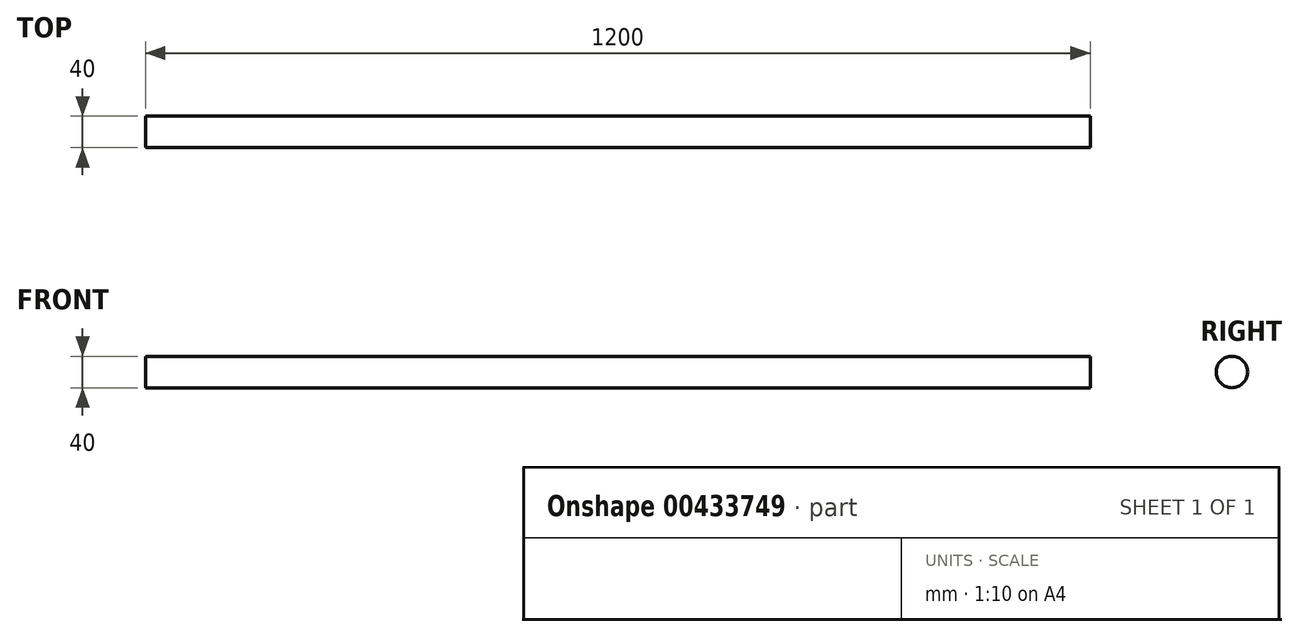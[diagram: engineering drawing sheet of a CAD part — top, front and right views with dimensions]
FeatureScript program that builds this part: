
annotation { "Feature Type Name" : "Feature", "Feature Type Description" : "" }
export const myFeature = defineFeature(function(context is Context, id is Id, definition is map)
    precondition{}
    {
        {
            var Q0;
            Q0=qCreatedBy(makeId("Front.planeOp"),FACE);
            var sketch = newSketch(context, id + "F0", { "sketchPlane" : qUnion([Q0])});
            skLineSegment(sketch, "E0.bottom", {"start": v(-558.88, -42.5) * mm, "end": v(641.12, -42.5) * mm});
            skLineSegment(sketch, "E0.top", {"start": v(-558.88, -82.5) * mm, "end": v(641.12, -82.5) * mm});
            skLineSegment(sketch, "E0.left", {"start": v(-558.88, -42.5) * mm, "end": v(-558.88, -82.5) * mm});
            skLineSegment(sketch, "E0.right", {"start": v(641.12, -42.5) * mm, "end": v(641.12, -82.5) * mm});
            skSolve(sketch);
        }
        {
            var Q0;
            Q0 = qSketchRegion(id + "F0", true);
            extrude(context, id + "F1", {"entities" : qUnion([Q0]), "depth" : 40 * mm, "offsetDistance" : 25 * mm});
        }
        {
            var Q0;
            Q0=makeQuery(id+"F1.opExtrude","CAP_EDGE",EDGE,{"disambiguationData":[OSD([sQuery(id+"F0.wireOp",EDGE,"E0.bottom")])],"isStart":false});
            var Q1;
            Q1=makeQuery(id+"F1.opExtrude","CAP_EDGE",EDGE,{"disambiguationData":[OSD([sQuery(id+"F0.wireOp",EDGE,"E0.bottom")])],"isStart":true});
            var Q2;
            Q2=makeQuery(id+"F1.opExtrude","CAP_EDGE",EDGE,{"disambiguationData":[OSD([sQuery(id+"F0.wireOp",EDGE,"E0.top")])],"isStart":false});
            var Q3;
            Q3=makeQuery(id+"F1.opExtrude","CAP_EDGE",EDGE,{"disambiguationData":[OSD([sQuery(id+"F0.wireOp",EDGE,"E0.top")])],"isStart":true});
            fillet(context, id + "F2", {"entities" : qUnion([Q0, Q1, Q2, Q3]), "radius" : 20 * mm, "tangentPropagation" : true, "allowEdgeOverflow" : false});
        }
    });
